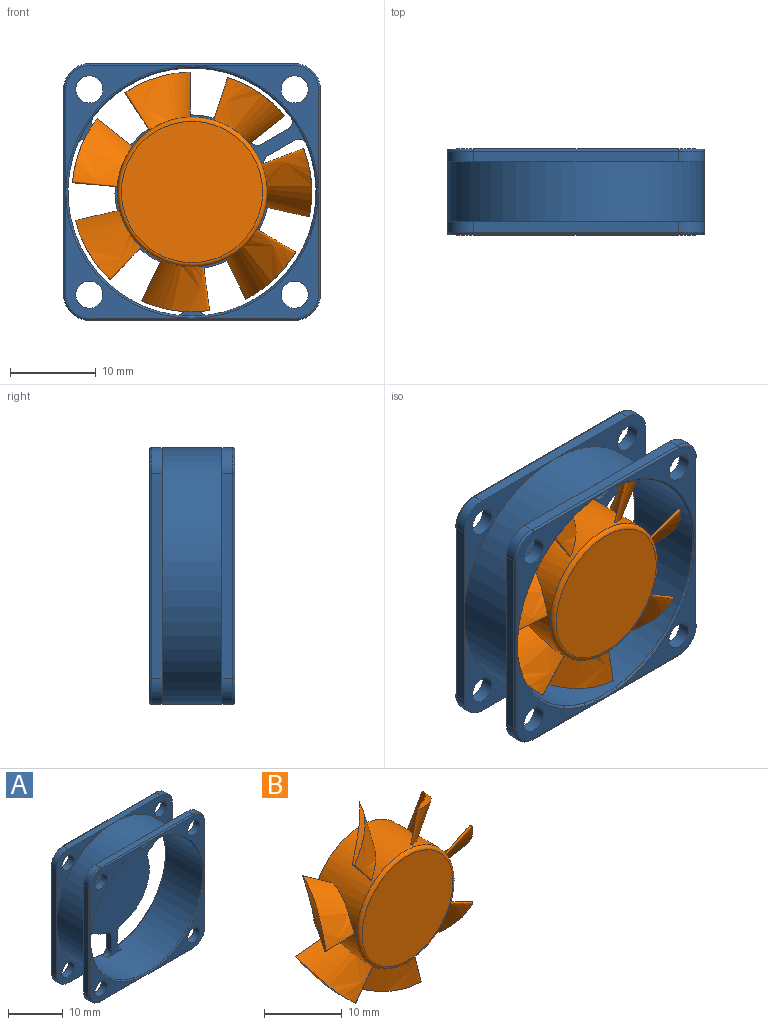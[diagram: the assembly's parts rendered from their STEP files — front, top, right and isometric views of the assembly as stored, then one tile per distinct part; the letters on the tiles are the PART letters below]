
ASSEMBLY  parts=2 mates=1
PART A: 102 faces, bbox 32.3x10x32.3 mm
  f0: plane 14.75x14.75mm, normal (0,-1,0), area 37mm2, adj f85,f87,f89,f93,f99
  f1: plane 14.75x14.75mm, normal (0,-1,0), area 37mm2, adj f85,f86,f88,f93,f100
  f2: plane 14.75x14.75mm, normal (0,-1,0), area 37mm2, adj f88,f90,f92,f93,f101
  f3: cylinder r=14.5mm len=29mm, axis (0,-1,0), area 851.4mm2, adj f31,f41,f42,f43,f44,f45,f46,f60
  f4: cylinder r=15mm len=30mm, axis (0,-1,0), area 659.7mm2, adj f5,f6,f7,f16,f23,f25,f28,f30
  f5: plane 15x15mm, normal (0,1,0), area 38.3mm2, adj f4,f8,f9,f10,f101
  f6: plane 15x15mm, normal (0,1,0), area 38.3mm2, adj f4,f10,f11,f12,f100
  f7: plane 15x15mm, normal (0,1,0), area 38.3mm2, adj f4,f12,f13,f14,f99
  f8: plane 24x1.25mm, normal (0,0,-1), area 30mm2, adj f5,f9,f15,f16,f92
  f9: cylinder r=3mm len=3mm, axis (0,-1,0), area 5.9mm2, adj f5,f8,f10,f90
  f10: plane 24x1.25mm, normal (1,0,0), area 30mm2, adj f5,f6,f9,f11,f88
  f11: cylinder r=3mm len=3mm, axis (0,-1,0), area 5.9mm2, adj f6,f10,f12,f86
  f12: plane 24x1.25mm, normal (0,0,1), area 30mm2, adj f6,f7,f11,f13,f85
  f13: cylinder r=3mm len=3mm, axis (0,-1,0), area 5.9mm2, adj f7,f12,f14,f87
  f14: plane 24x1.25mm, normal (-1,0,0), area 30mm2, adj f7,f13,f15,f16,f89
  f15: cylinder r=3mm len=3mm, axis (0,-1,0), area 5.9mm2, adj f8,f14,f16,f91
  f16: plane 15x15mm, normal (0,1,0), area 38.3mm2, adj f4,f8,f14,f15,f98
  f17: plane 14.75x14.75mm, normal (0,-1,0), area 37mm2, adj f89,f91,f92,f93,f98
  f18: plane 29.5x29.5mm, normal (0,1,0), area 410.6mm2, adj f53,f54,f55,f56,f57,f58,f59,f60
  f19: plane 24x1.25mm, normal (-1,0,0), area 30mm2, adj f20,f27,f28,f30,f81
  f20: cylinder r=3mm len=3mm, axis (0,1,0), area 5.9mm2, adj f19,f29,f30,f79
  f21: cylinder r=3mm len=3mm, axis (0,1,0), area 5.9mm2, adj f22,f23,f29,f78
  f22: plane 24x1.25mm, normal (1,0,0), area 30mm2, adj f21,f23,f24,f25,f80
  f23: plane 15x15mm, normal (0,-1,0), area 38.3mm2, adj f4,f21,f22,f29,f97
  f24: cylinder r=3mm len=3mm, axis (0,1,0), area 5.9mm2, adj f22,f25,f26,f82
  f25: plane 15x15mm, normal (0,-1,0), area 38.3mm2, adj f4,f22,f24,f26,f96
  f26: plane 24x1.25mm, normal (0,0,-1), area 30mm2, adj f24,f25,f27,f28,f84
  f27: cylinder r=3mm len=3mm, axis (0,1,0), area 5.9mm2, adj f19,f26,f28,f83
  f28: plane 15x15mm, normal (0,-1,0), area 38.3mm2, adj f4,f19,f26,f27,f95
  f29: plane 24x1.25mm, normal (0,0,1), area 30mm2, adj f20,f21,f23,f30,f77
  f30: plane 15x15mm, normal (0,-1,0), area 38.3mm2, adj f4,f19,f20,f29,f94
  f31: plane 26.78x23.5mm, normal (0,-1,0), area 281.8mm2, adj f3,f32,f33,f34,f35,f36,f37,f38
  f32: plane 3.07x1.77mm, normal (0.5,0,-0.87), area 4.4mm2, adj f31,f41,f47,f73
  f33: cylinder r=9mm len=11.93mm, axis (0,1,0), area 19.6mm2, adj f31,f47,f48,f69
  f34: plane 3.07x1.77mm, normal (-0.5,0,-0.87), area 4.4mm2, adj f31,f44,f50,f64
  f35: plane 3.54x1.25mm, normal (-1,0,0), area 4.4mm2, adj f31,f45,f49,f65
  f36: plane 3.07x1.77mm, normal (-0.5,0,0.87), area 4.4mm2, adj f31,f42,f52,f56
  f37: plane 3.07x1.77mm, normal (0.5,0,0.87), area 4.4mm2, adj f31,f43,f51,f57
  f38: cylinder r=9mm len=11.93mm, axis (0,1,0), area 19.6mm2, adj f31,f49,f50,f61
  f39: cylinder r=9mm len=13.77mm, axis (0,1,0), area 19.6mm2, adj f31,f51,f52,f53
  f40: plane 3.54x1.25mm, normal (1,0,0), area 4.4mm2, adj f31,f46,f48,f72
  f41: cylinder r=1mm len=1.42mm, axis (0,-1,0), area 2.1mm2, adj f3,f31,f32,f75
  f42: cylinder r=1mm len=1.47mm, axis (0,-1,0), area 2.1mm2, adj f3,f31,f36,f58
  f43: cylinder r=1mm len=1.47mm, axis (0,-1,0), area 2.1mm2, adj f3,f31,f37,f59
  f44: cylinder r=1mm len=1.42mm, axis (0,-1,0), area 2.1mm2, adj f3,f31,f34,f66
  f45: cylinder r=1mm len=1.25mm, axis (0,-1,0), area 2.1mm2, adj f3,f31,f35,f67
  f46: cylinder r=1mm len=1.25mm, axis (0,-1,0), area 2.1mm2, adj f3,f31,f40,f74
  f47: cylinder r=1mm len=1.25mm, axis (0,1,0), area 1.7mm2, adj f31,f32,f33,f71
  f48: cylinder r=1mm len=1.25mm, axis (0,1,0), area 1.7mm2, adj f31,f33,f40,f70
  f49: cylinder r=1mm len=1.25mm, axis (0,1,0), area 1.7mm2, adj f31,f35,f38,f63
  f50: cylinder r=1mm len=1.25mm, axis (0,1,0), area 1.7mm2, adj f31,f34,f38,f62
  f51: cylinder r=1mm len=1.27mm, axis (0,1,0), area 1.7mm2, adj f31,f37,f39,f55
  f52: cylinder r=1mm len=1.27mm, axis (0,1,0), area 1.7mm2, adj f31,f36,f39,f54
  f53: torus R=8.75mm, axis (0,-1,0), area 6.1mm2, adj f18,f39,f54,f55
  f54: torus R=1.25mm, axis (0,-1,0), area 0.6mm2, adj f18,f52,f53,f56
  f55: torus R=1.25mm, axis (0,-1,0), area 0.6mm2, adj f18,f51,f53,f57
  f56: cylinder r=0.25mm len=3.19mm, axis (-0.87,0,-0.5), area 1.4mm2, adj f18,f36,f54,f58
  f57: cylinder r=0.25mm len=3.19mm, axis (-0.87,0,0.5), area 1.4mm2, adj f18,f37,f55,f59
  f58: torus R=1.25mm, axis (0,-1,0), area 0.7mm2, adj f18,f42,f56,f60
  f59: torus R=1.25mm, axis (0,-1,0), area 0.7mm2, adj f18,f43,f57,f60
  f60: torus R=14.75mm, axis (0,-1,0), area 10.5mm2, adj f3,f18,f58,f59
  f61: torus R=8.75mm, axis (0,-1,0), area 6.1mm2, adj f18,f38,f62,f63
  f62: torus R=1.25mm, axis (0,-1,0), area 0.6mm2, adj f18,f50,f61,f64
  f63: torus R=1.25mm, axis (0,-1,0), area 0.6mm2, adj f18,f49,f61,f65
  f64: cylinder r=0.25mm len=3.19mm, axis (0.87,0,-0.5), area 1.4mm2, adj f18,f34,f62,f66
  f65: cylinder r=0.25mm len=3.54mm, axis (0,0,-1), area 1.4mm2, adj f18,f35,f63,f67
  f66: torus R=1.25mm, axis (0,-1,0), area 0.7mm2, adj f18,f44,f64,f68
  f67: torus R=1.25mm, axis (0,-1,0), area 0.7mm2, adj f18,f45,f65,f68
  f68: torus R=14.75mm, axis (0,-1,0), area 10.5mm2, adj f3,f18,f66,f67
  f69: torus R=8.75mm, axis (0,-1,0), area 6.1mm2, adj f18,f33,f70,f71
  f70: torus R=1.25mm, axis (0,-1,0), area 0.6mm2, adj f18,f48,f69,f72
  f71: torus R=1.25mm, axis (0,-1,0), area 0.6mm2, adj f18,f47,f69,f73
  f72: cylinder r=0.25mm len=3.54mm, axis (0,0,1), area 1.4mm2, adj f18,f40,f70,f74
  f73: cylinder r=0.25mm len=3.19mm, axis (0.87,0,0.5), area 1.4mm2, adj f18,f32,f71,f75
  f74: torus R=1.25mm, axis (0,-1,0), area 0.7mm2, adj f18,f46,f72,f76
  f75: torus R=1.25mm, axis (0,-1,0), area 0.7mm2, adj f18,f41,f73,f76
  f76: torus R=14.75mm, axis (0,-1,0), area 10.5mm2, adj f3,f18,f74,f75
  f77: cylinder r=0.25mm len=24mm, axis (-1,0,0), area 9.4mm2, adj f18,f29,f78,f79
  f78: torus R=2.75mm, axis (0,-1,0), area 1.8mm2, adj f18,f21,f77,f80
  f79: torus R=2.75mm, axis (0,-1,0), area 1.8mm2, adj f18,f20,f77,f81
  f80: cylinder r=0.25mm len=24mm, axis (0,0,1), area 9.4mm2, adj f18,f22,f78,f82
  f81: cylinder r=0.25mm len=24mm, axis (0,0,-1), area 9.4mm2, adj f18,f19,f79,f83
  f82: torus R=2.75mm, axis (0,-1,0), area 1.8mm2, adj f18,f24,f80,f84
  f83: torus R=2.75mm, axis (0,-1,0), area 1.8mm2, adj f18,f27,f81,f84
  f84: cylinder r=0.25mm len=24mm, axis (1,0,0), area 9.4mm2, adj f18,f26,f82,f83
  f85: cylinder r=0.25mm len=24mm, axis (-1,0,0), area 9.4mm2, adj f0,f1,f12,f86,f87
  f86: torus R=2.75mm, axis (0,-1,0), area 1.8mm2, adj f1,f11,f85,f88
  f87: torus R=2.75mm, axis (0,-1,0), area 1.8mm2, adj f0,f13,f85,f89
  f88: cylinder r=0.25mm len=24mm, axis (0,0,1), area 9.4mm2, adj f1,f2,f10,f86,f90
  f89: cylinder r=0.25mm len=24mm, axis (0,0,-1), area 9.4mm2, adj f0,f14,f17,f87,f91
  f90: torus R=2.75mm, axis (0,-1,0), area 1.8mm2, adj f2,f9,f88,f92
  f91: torus R=2.75mm, axis (0,-1,0), area 1.8mm2, adj f15,f17,f89,f92
  f92: cylinder r=0.25mm len=24mm, axis (1,0,0), area 9.4mm2, adj f2,f8,f17,f90,f91
  f93: torus R=14.75mm, axis (0,-1,0), area 36mm2, adj f0,f1,f2,f3,f17
  f94: cylinder r=1.6mm len=3.2mm, axis (0,-1,0), area 15.1mm2, adj f18,f30
  f95: cylinder r=1.6mm len=3.2mm, axis (0,-1,0), area 15.1mm2, adj f18,f28
  f96: cylinder r=1.6mm len=3.2mm, axis (0,-1,0), area 15.1mm2, adj f18,f25
  f97: cylinder r=1.6mm len=3.2mm, axis (0,-1,0), area 15.1mm2, adj f18,f23
  f98: cylinder r=1.6mm len=3.2mm, axis (0,-1,0), area 15.1mm2, adj f16,f17
  f99: cylinder r=1.6mm len=3.2mm, axis (0,-1,0), area 15.1mm2, adj f0,f7
  f100: cylinder r=1.6mm len=3.2mm, axis (0,-1,0), area 15.1mm2, adj f1,f6
  f101: cylinder r=1.6mm len=3.2mm, axis (0,-1,0), area 15.1mm2, adj f2,f5
PART B: 25 faces, bbox 29.2x8.5x28.7 mm
  f0: bspline ~8.86x8.5mm, area 49.5mm2, adj f1,f16,f23
  f1: bspline ~8.83x8.41mm, area 45.4mm2, adj f0,f16,f23
  f2: bspline ~8.18x6.98mm, area 49.5mm2, adj f3,f16,f22
  f3: bspline ~8.09x6.96mm, area 45.4mm2, adj f2,f16,f22
  f4: bspline ~8.21x8.16mm, area 49.5mm2, adj f5,f16,f21
  f5: bspline ~8.19x8.06mm, area 45.4mm2, adj f4,f16,f21
  f6: bspline ~8.82x7.89mm, area 49.5mm2, adj f7,f16,f20
  f7: bspline ~8.78x7.84mm, area 45.4mm2, adj f6,f16,f20
  f8: bspline ~8.18x7.14mm, area 49.5mm2, adj f9,f16,f19
  f9: bspline ~8.07x7.13mm, area 45.4mm2, adj f8,f16,f19
  f10: bspline ~9.07x8.4mm, area 49.5mm2, adj f11,f16,f18
  f11: bspline ~9.25x8.61mm, area 45.4mm2, adj f10,f16,f18
  f12: bspline ~8.27x6.24mm, area 45.5mm2, adj f13,f16,f17
  f13: bspline ~8.39x6.62mm, area 49.8mm2, adj f12,f16,f17
  f14: plane 17.5x17.5mm, normal (0,1,0), area 240.5mm2, adj f16
  f15: plane 16.5x16.5mm, normal (0,-1,0), area 213.8mm2, adj f24
  f16: cylinder r=8.75mm len=17.5mm, axis (0,-1,0), area 418.4mm2, adj f0,f1,f2,f3,f4,f5,f6,f7
  f17: cylinder r=14mm len=8.01mm, axis (0,-1,0), area 6.4mm2, adj f12,f13
  f18: cylinder r=14mm len=6.44mm, axis (0,-1,0), area 6.4mm2, adj f10,f11
  f19: cylinder r=14mm len=7.89mm, axis (0,-1,0), area 6.4mm2, adj f8,f9
  f20: cylinder r=14mm len=7.05mm, axis (0,-1,0), area 6.4mm2, adj f6,f7
  f21: cylinder r=14mm len=7.38mm, axis (0,-1,0), area 6.4mm2, adj f4,f5
  f22: cylinder r=14mm len=7.72mm, axis (0,-1,0), area 6.4mm2, adj f2,f3
  f23: cylinder r=14mm len=6.49mm, axis (0,-1,0), area 6.4mm2, adj f0,f1
  f24: torus R=8.25mm, axis (0,-1,0), area 42.3mm2, adj f15,f16
PLACE A at identity fixed
PLACE B rot(axis=(0,1,0),56.9deg) t=(0,0,0)mm
MATE revolute B.f16 <-> A.f3  axis (0,1,0) through (0,8.5,0)mm
